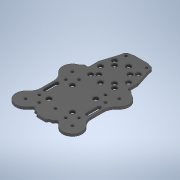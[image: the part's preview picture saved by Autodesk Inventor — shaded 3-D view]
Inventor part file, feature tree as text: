
AUTODESK INVENTOR PART (.ipt)
format: ipt  version: 2020 (Build 240168000, 168)  size: 478,208 bytes
history: native  units: in
note: dims shown in document units (in); Inventor stores cm internally (conversion verified against a paired STEP export)
features: sketch x5, extrude x3, projected_geometry x3
ambient origin geometry x8: Origin, YZ Plane, XZ Plane, XY Plane, X Axis, Y Axis, Z Axis, Center Point
bodies: Solid2 (feature_tree), Solid1 (feature_tree)
feature tree (11):
  extrude  "Extrusion1"  Depth=0.2362in
  sketch  "Sketch3"  dims[d3=0.2362in d4=0.2362in]
  sketch  "Sketch4"  dims[d5=0.2362in d6=0.2362in]
  extrude  "Extrusion2"  Depth=0.2362in
  extrude  "Extrusion3"  Depth=0.2362in
  sketch  "Sketch2"  dims[d1=0.2362in d2=0.2362in]
  projected_geometry  "Projected Loop2"
  projected_geometry  "Projected Loop3"
  projected_geometry  "Projected Loop4"
  sketch  "Sketch5"  dims[d7=0.2362in]
  sketch  "Sketch6"  dims[d8=0.2362in d9=0.2362in d10=0.2362in d11=0.2362in d12=0.2362in d13=0.3937in d14=0.0in d27=0.3937in d28=0.0in d29=0.2362in d30=0.2362in d31=0.2362in d32=0.2362in d33=0.2362in d34=1.0039in d35=1.0039in d36=1.0039in d37=1.0039in d38=1.4197in d39=0.3937in d40=0.0in]
